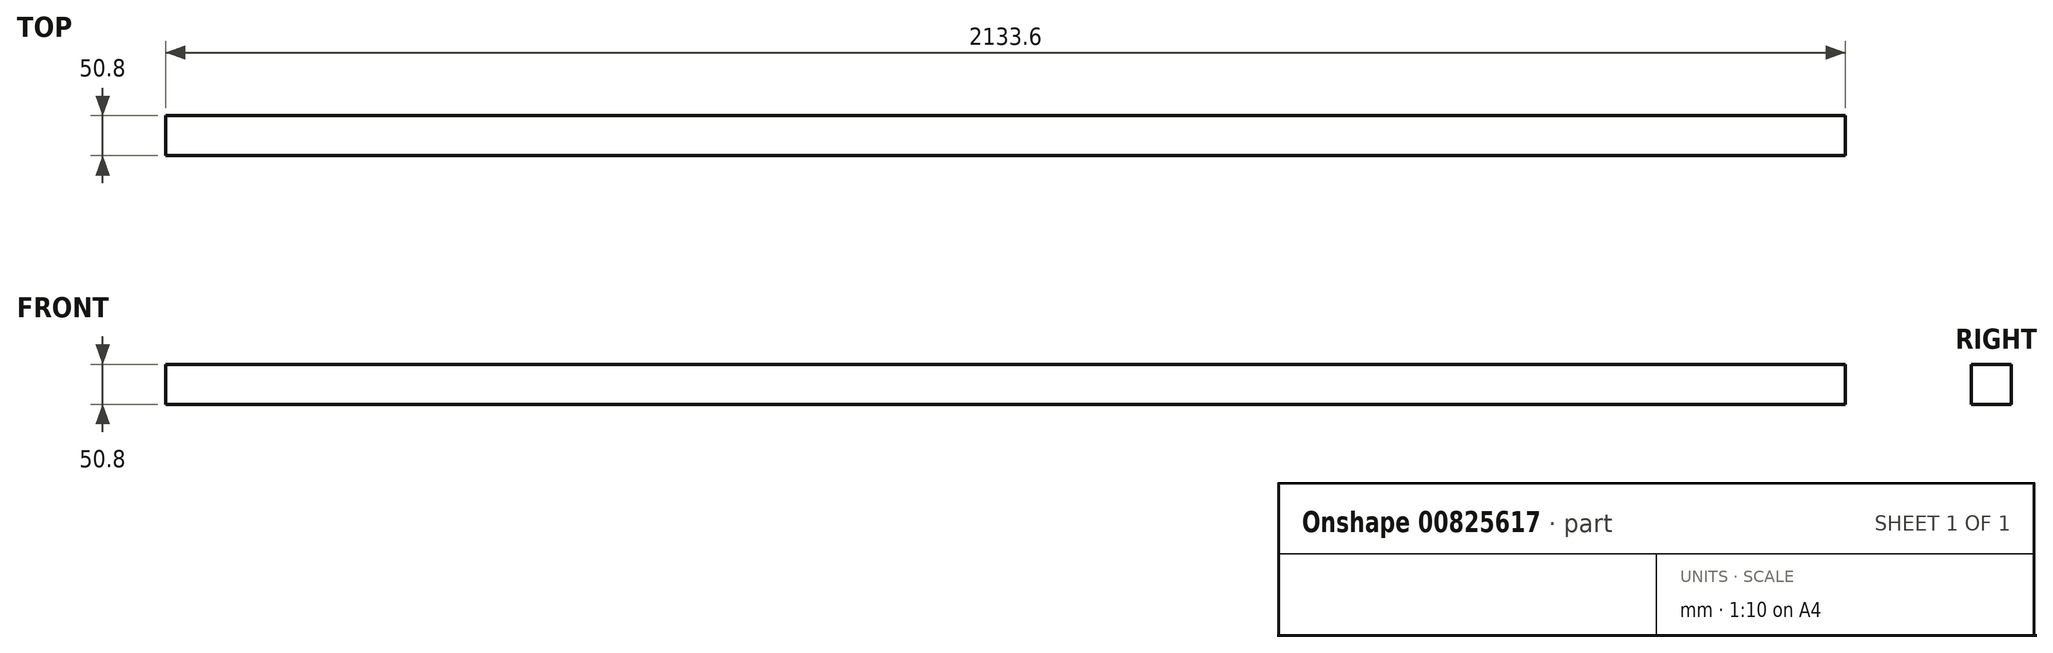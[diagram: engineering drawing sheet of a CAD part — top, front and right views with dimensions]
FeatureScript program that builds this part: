
annotation { "Feature Type Name" : "Feature", "Feature Type Description" : "" }
export const myFeature = defineFeature(function(context is Context, id is Id, definition is map)
    precondition{}
    {
        {
            var Q0;
            Q0=qCreatedBy(makeId("Right.planeOp"),FACE);
            var sketch = newSketch(context, id + "F0", { "sketchPlane" : qUnion([Q0])});
            skLineSegment(sketch, "E0.bottom", {"start": v(-34.43, -4.83) * mm, "end": v(16.37, -4.83) * mm});
            skLineSegment(sketch, "E0.top", {"start": v(-34.43, 45.97) * mm, "end": v(16.37, 45.97) * mm});
            skLineSegment(sketch, "E0.left", {"start": v(-34.43, -4.83) * mm, "end": v(-34.43, 45.97) * mm});
            skLineSegment(sketch, "E0.right", {"start": v(16.37, -4.83) * mm, "end": v(16.37, 45.97) * mm});
            skSolve(sketch);
        }
        {
            var Q0;
            Q0 = qSketchRegion(id + "F0", true);
            extrude(context, id + "F1", {"entities" : qUnion([Q0]), "depth" : 2133.6 * mm, "offsetDistance" : 25.4 * mm});
        }
    });
